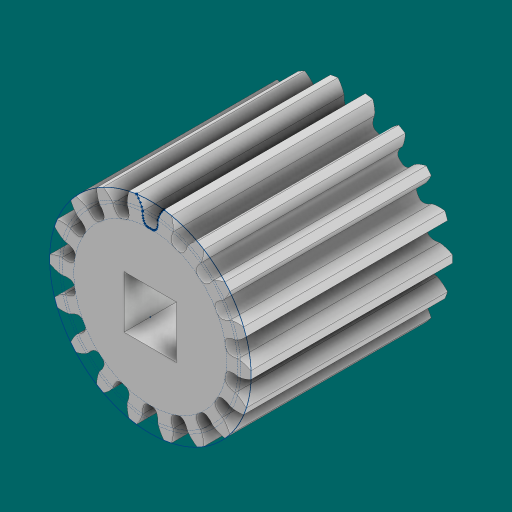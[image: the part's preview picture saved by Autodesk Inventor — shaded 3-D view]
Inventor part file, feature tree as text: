
AUTODESK INVENTOR PART (.ipt)
format: ipt  version: 2023.1 (Build 271208000, 208)  size: 804,352 bytes
history: native  units: in
note: dims shown in document units (in); Inventor stores cm internally (conversion verified against a paired STEP export)
features: extrude x5, sketch x4, pattern_circular x1, chamfer x1, projected_geometry x1
ambient origin geometry x8: Origin, YZ Plane, XZ Plane, XY Plane, X Axis, Y Axis, Z Axis, Center Point
bodies: Solid1 (feature_tree)
feature tree (12):
  sketch  "Sketch1"  dims[d0=1.0in d1=0.0in]
  extrude  "Extrusion1"  TaperAngle=0.0deg  [1 undecoded]
  extrude  "Extrusion2"  Depth=7.0866in TaperAngle=360.0deg
  pattern_circular  "Circular Pattern1"  [2 undecoded]
  extrude  "Extrusion3"  Depth=0.05in TaperAngle=0.0deg
  extrude  "Extrusion4"  Depth=0.05in
  extrude  "Extrusion5"  Depth=0.05in TaperAngle=0.0deg
  chamfer  "Chamfer2"  Distance=0.0118in Angle=45.0deg
  sketch  "Sketch2"  dims[d2=0.0in d3=0.0in d4=7.0866in d5=360.0deg]
  sketch  "Sketch3"  dims[d9=0.0in d10=0.0in]
  sketch  "Sketch4"  dims[d11=0.26in d12=0.26in d13=0.9in d14=0.0in d18=0.33in d19=0.05in d20=0.0in d21=0.0118in d22=0.125in d23=45.0deg d24=0.18in d25=0.18in]
  projected_geometry  "Projected Loop1"
note: 3 required parameter values undecoded (feature->parameter linkage not recoverable at this tier; creation-order binding heuristic only, values carry confidence <= 0.55)
